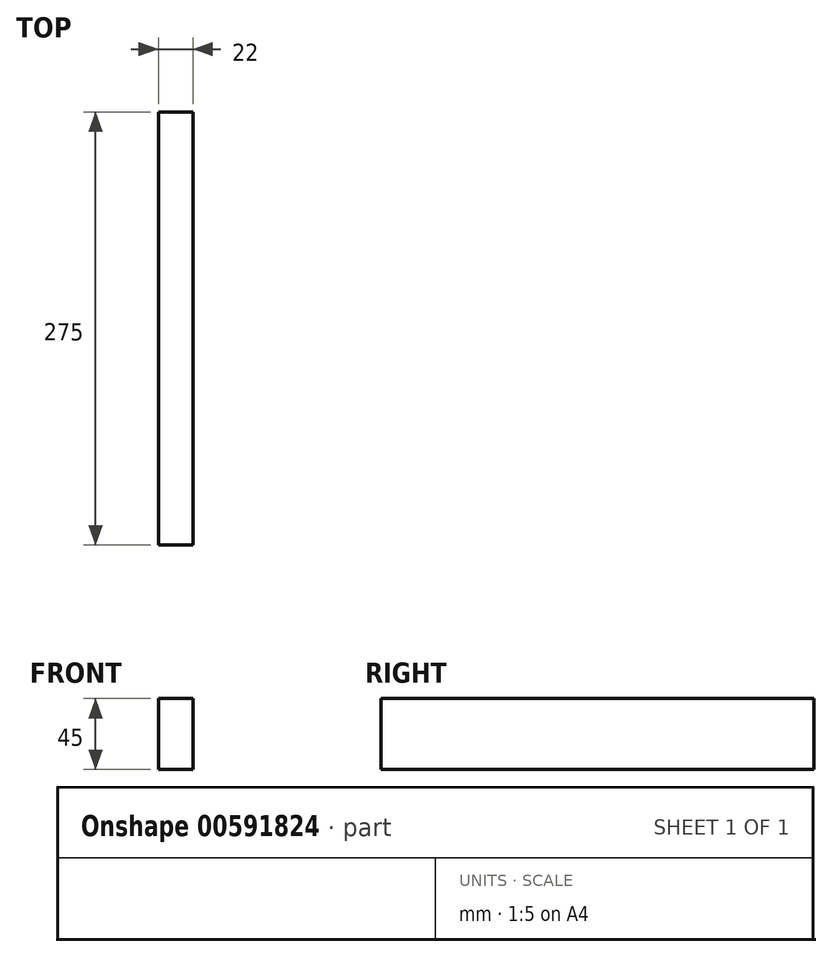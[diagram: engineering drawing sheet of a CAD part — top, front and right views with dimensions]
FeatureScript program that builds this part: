
annotation { "Feature Type Name" : "Feature", "Feature Type Description" : "" }
export const myFeature = defineFeature(function(context is Context, id is Id, definition is map)
    precondition{}
    {
        {
            var Q0;
            Q0=qCreatedBy(makeId("Front.planeOp"),FACE);
            var sketch = newSketch(context, id + "F0", { "sketchPlane" : qUnion([Q0])});
            skLineSegment(sketch, "E0.bottom", {"start": v(0, 0) * mm, "end": v(22, 0) * mm});
            skLineSegment(sketch, "E0.top", {"start": v(0, 45) * mm, "end": v(22, 45) * mm});
            skLineSegment(sketch, "E0.left", {"start": v(0, 0) * mm, "end": v(0, 45) * mm});
            skLineSegment(sketch, "E0.right", {"start": v(22, 0) * mm, "end": v(22, 45) * mm});
            skSolve(sketch);
        }
        {
            var Q0;
            Q0=qSketchRegion(id+"F0",true);
            extrude(context, id + "F1", {"entities" : qUnion([Q0]), "depth" : 275 * mm, "offsetDistance" : 25 * mm});
        }
    });
